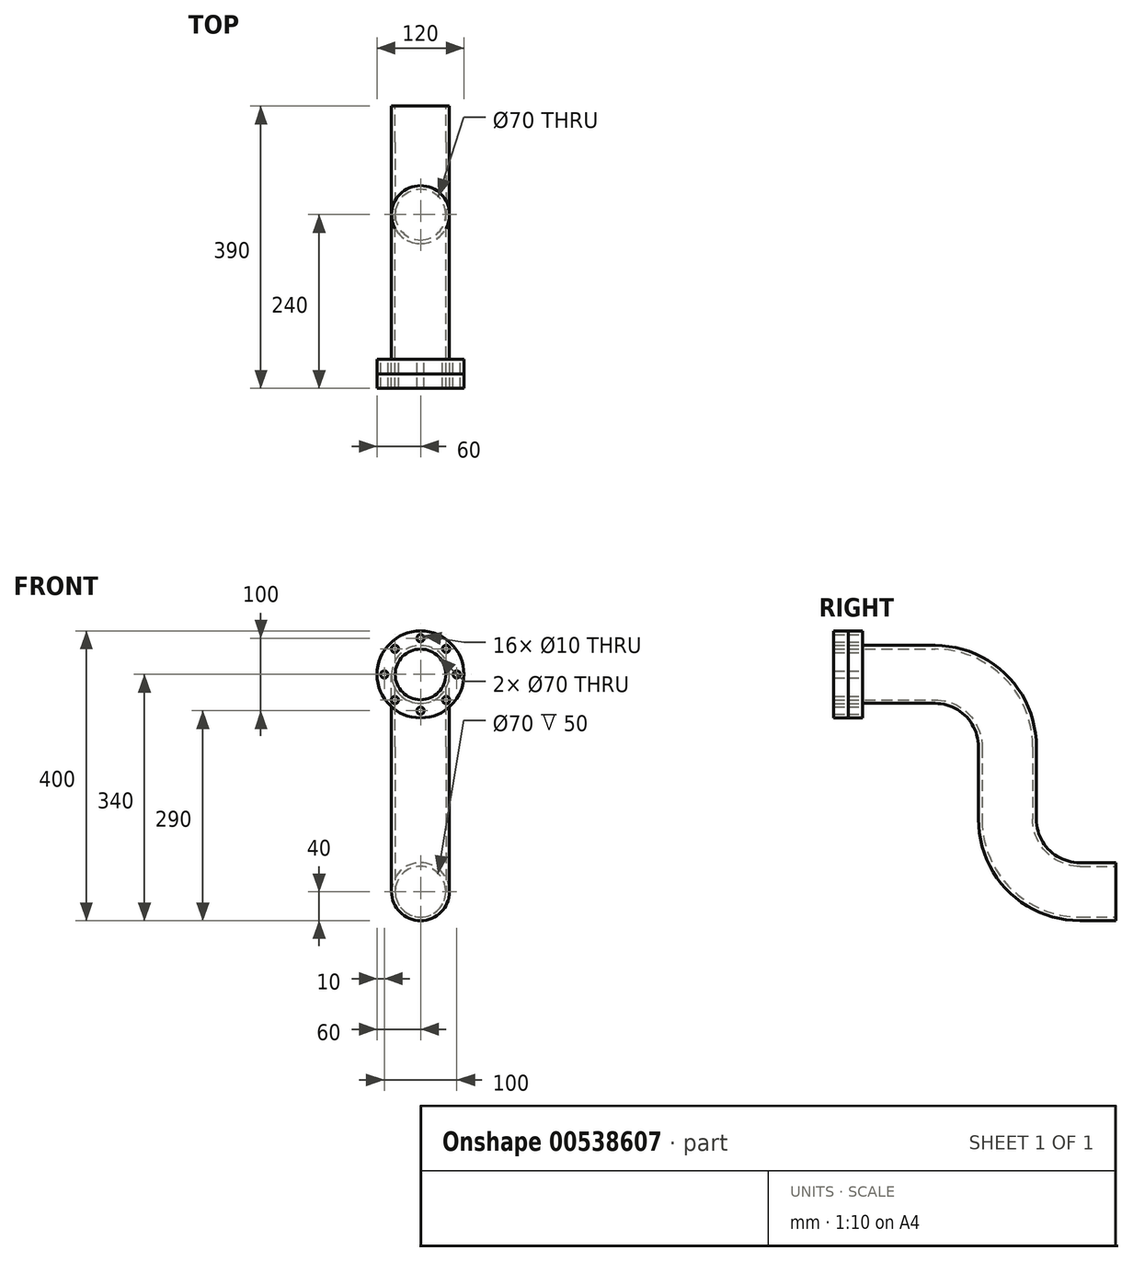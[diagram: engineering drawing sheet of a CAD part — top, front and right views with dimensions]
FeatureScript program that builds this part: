
annotation { "Feature Type Name" : "Feature", "Feature Type Description" : "" }
export const myFeature = defineFeature(function(context is Context, id is Id, definition is map)
    precondition{}
    {
        {
            var Q0;
            Q0=qCreatedBy(makeId("Front.planeOp"),FACE);
            var sketch = newSketch(context, id + "F0", { "sketchPlane" : qUnion([Q0])});
            skCircle(sketch, "E0", {"center": v(0, 0) * mm, "radius": 60 * mm});
            skCircle(sketch, "E1", {"center": v(0, 50) * mm, "radius": 5 * mm});
            skCircle(sketch, "E2.1.0", {"center": v(-35.36, 35.36) * mm, "radius": 5 * mm});
            skCircle(sketch, "E2.2.0", {"center": v(-50, 0) * mm, "radius": 5 * mm});
            skCircle(sketch, "E2.3.0", {"center": v(-35.36, -35.36) * mm, "radius": 5 * mm});
            skCircle(sketch, "E2.4.0", {"center": v(0, -50) * mm, "radius": 5 * mm});
            skCircle(sketch, "E2.5.0", {"center": v(35.36, -35.36) * mm, "radius": 5 * mm});
            skCircle(sketch, "E2.6.0", {"center": v(50, 0) * mm, "radius": 5 * mm});
            skCircle(sketch, "E2.7.0", {"center": v(35.36, 35.36) * mm, "radius": 5 * mm});
            skCircle(sketch, "E3", {"center": v(0, 0) * mm, "radius": 35 * mm});
            skSolve(sketch);
        }
        {
            var Q0;
            Q0 = qSketchRegion(id + "F0", true);
            extrude(context, id + "F1", {"entities" : qUnion([Q0]), "depth" : 20 * mm, "offsetDistance" : 25 * mm});
        }
        {
            var Q0;
            Q0=qCreatedBy(makeId("Front.planeOp"),FACE);
            var sketch = newSketch(context, id + "F2", { "sketchPlane" : qUnion([Q0])});
            skCircle(sketch, "E4", {"center": v(0, 0) * mm, "radius": 40 * mm});
            skCircle(sketch, "E5", {"center": v(0, 0) * mm, "radius": 35 * mm});
            skSolve(sketch);
        }
        {
            var Q0;
            Q0=qCreatedBy(makeId("Right.planeOp"),FACE);
            var sketch = newSketch(context, id + "F3", { "sketchPlane" : qUnion([Q0])});
            skLineSegment(sketch, "E6", {"start": v(0, 0) * mm, "end": v(100, 0) * mm});
            skLineSegment(sketch, "E7", {"start": v(200, -100) * mm, "end": v(200, -200) * mm});
            skLineSegment(sketch, "E8", {"start": v(300, -300) * mm, "end": v(350, -300) * mm});
            skPoint(sketch, "E9.visualSharp", {"position": v(200, 0) * mm});
            skArc(sketch, "E9.filletArc", {"start": v(200, -100) * mm, "mid": v(170.71, -29.29) * mm, "end": v(100, 0) * mm});
            skPoint(sketch, "E10.visualSharp", {"position": v(200, -300) * mm});
            skArc(sketch, "E10.filletArc", {"start": v(200, -200) * mm, "mid": v(229.29, -270.71) * mm, "end": v(300, -300) * mm});
            skSolve(sketch);
        }
        {
            var Q0;
            Q0=makeQuery(id+"F2.imprint","IMPRINT",FACE,{"disambiguationData":[TD([[makeQuery(id+"F2.imprint","IMPRINT",EDGE,{"derivedFrom":sQuery(id+"F2.wireOp",EDGE,"E4")}),1.0]])]});
            var Q1;
            Q1=sQuery(id+"F3.wireOp",EDGE,"E6");
            var Q2;
            Q2=sQuery(id+"F3.wireOp",EDGE,"E9.filletArc");
            var Q3;
            Q3=sQuery(id+"F3.wireOp",EDGE,"E7");
            var Q4;
            Q4=sQuery(id+"F3.wireOp",EDGE,"E10.filletArc");
            var Q5;
            Q5=sQuery(id+"F3.wireOp",EDGE,"E8");
            sweep(context, id + "F4", {"operationType" : NewBodyOperationType.ADD, "profiles" : qUnion([Q0]), "path" : qUnion([Q1, Q2, Q3, Q4, Q5])});
        }
        {
            var Q0;
            Q0=makeQuery(id+"F1.opExtrude","CAP_FACE",FACE,{"disambiguationData":[OSD([sQuery(id+"F0.wireOp",EDGE,"E0"),sQuery(id+"F0.wireOp",EDGE,"E1"),sQuery(id+"F0.wireOp",EDGE,"E2.1.0"),sQuery(id+"F0.wireOp",EDGE,"E2.2.0"),sQuery(id+"F0.wireOp",EDGE,"E2.3.0"),sQuery(id+"F0.wireOp",EDGE,"E2.4.0"),sQuery(id+"F0.wireOp",EDGE,"E2.5.0"),sQuery(id+"F0.wireOp",EDGE,"E2.6.0"),sQuery(id+"F0.wireOp",EDGE,"E2.7.0"),sQuery(id+"F0.wireOp",EDGE,"E3")])],"isStart":false});
            extrude(context, id + "F5", {"entities" : qUnion([Q0]), "depth" : 20 * mm, "offsetDistance" : 25 * mm});
        }
    });
